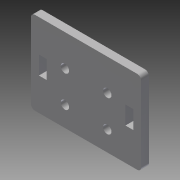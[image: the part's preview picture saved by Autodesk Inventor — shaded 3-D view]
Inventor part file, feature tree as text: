
AUTODESK INVENTOR PART (.ipt)
format: ipt  version: 2013 (Build 170138000, 138)  size: 114,688 bytes
history: native  units: in
note: dims shown in document units (in); Inventor stores cm internally (conversion verified against a paired STEP export)
features: sketch x4, reference x4, extrude x3, fillet x1
ambient origin geometry x8: Origin, YZ Plane, XZ Plane, XY Plane, X Axis, Y Axis, Z Axis, Center Point
bodies: Solid1 (feature_tree)
feature tree (12):
  extrude  "Extrusion1"  Depth=2.638in
  sketch  "Sketch2"  dims[d2=90.0deg d3=0.25in d4=0.0in d5=1.031in]
  extrude  "Extrusion2"  Depth=0.25in TaperAngle=0.0deg
  fillet  "Fillet1"  Radius=1.031in
  extrude  "Extrusion3"  Depth=0.577in
  sketch  "Sketch1"  dims[d0=3.5in d1=2.638in]
  sketch  "Sketch3"  dims[d6=0.25in d7=0.577in]
  sketch  "Sketch4"  dims[d8=0.25in d9=0.25in d10=0.25in d11=0.577in d12=1.0in d13=0.0in d14=0.125in d15=1.0in d16=0.0in]
  reference  "Reference1"
  reference  "Reference2"
  reference  "Reference3"
  reference  "Reference4"
